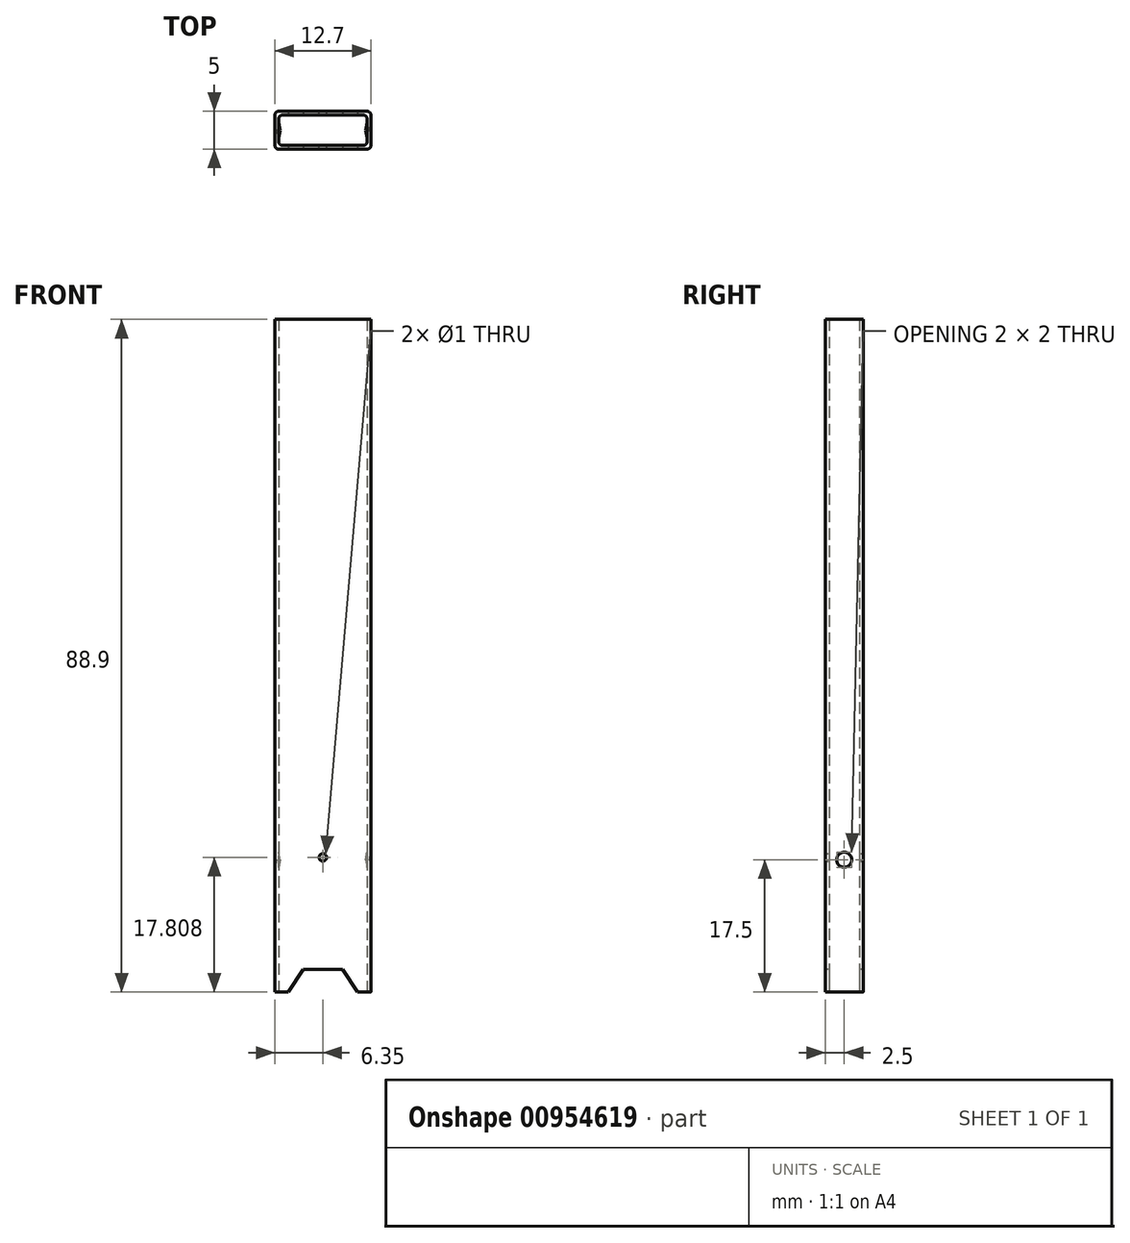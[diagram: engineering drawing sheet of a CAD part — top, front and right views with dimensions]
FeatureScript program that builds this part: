
annotation { "Feature Type Name" : "Feature", "Feature Type Description" : "" }
export const myFeature = defineFeature(function(context is Context, id is Id, definition is map)
    precondition{}
    {
        {
            var Q0;
            Q0=qCreatedBy(makeId("Top.planeOp"),FACE);
            var sketch = newSketch(context, id + "F0", { "sketchPlane" : qUnion([Q0])});
            skLineSegment(sketch, "E0.bottom", {"start": v(0.5, 0) * mm, "end": v(12.2, 0) * mm});
            skLineSegment(sketch, "E0.top", {"start": v(0.5, -5) * mm, "end": v(12.2, -5) * mm});
            skLineSegment(sketch, "E0.left", {"start": v(0, -0.5) * mm, "end": v(0, -4.5) * mm});
            skLineSegment(sketch, "E0.right", {"start": v(12.7, -0.5) * mm, "end": v(12.7, -4.5) * mm});
            skPoint(sketch, "E1.visualSharp", {"position": v(0, 0) * mm});
            skArc(sketch, "E1.filletArc", {"start": v(0.5, 0) * mm, "mid": v(0.15, -0.15) * mm, "end": v(0, -0.5) * mm});
            skPoint(sketch, "E2.visualSharp", {"position": v(0, -5) * mm});
            skArc(sketch, "E2.filletArc", {"start": v(0, -4.5) * mm, "mid": v(0.15, -4.85) * mm, "end": v(0.5, -5) * mm});
            skPoint(sketch, "E3.visualSharp", {"position": v(12.7, -5) * mm});
            skArc(sketch, "E3.filletArc", {"start": v(12.2, -5) * mm, "mid": v(12.55, -4.85) * mm, "end": v(12.7, -4.5) * mm});
            skPoint(sketch, "E4.visualSharp", {"position": v(12.7, 0) * mm});
            skArc(sketch, "E4.filletArc", {"start": v(12.7, -0.5) * mm, "mid": v(12.55, -0.15) * mm, "end": v(12.2, 0) * mm});
            skLineSegment(sketch, "E5.0", {"start": v(12.2, -0.5) * mm, "end": v(12.2, -0.5) * mm});
            skLineSegment(sketch, "E5.1", {"start": v(0.5, -0.5) * mm, "end": v(12.2, -0.5) * mm});
            skLineSegment(sketch, "E5.2", {"start": v(12.2, -0.5) * mm, "end": v(12.2, -4.5) * mm});
            skLineSegment(sketch, "E5.3", {"start": v(0.5, -0.5) * mm, "end": v(0.5, -0.5) * mm});
            skLineSegment(sketch, "E5.4", {"start": v(12.2, -4.5) * mm, "end": v(12.2, -4.5) * mm});
            skLineSegment(sketch, "E5.5", {"start": v(0.5, -4.5) * mm, "end": v(12.2, -4.5) * mm});
            skLineSegment(sketch, "E5.6", {"start": v(0.5, -4.5) * mm, "end": v(0.5, -4.5) * mm});
            skLineSegment(sketch, "E5.7", {"start": v(0.5, -0.5) * mm, "end": v(0.5, -4.5) * mm});
            skSolve(sketch);
        }
        {
            var Q0;
            Q0 = qSketchRegion(id + "F0", true);
            extrude(context, id + "F1", {"entities" : qUnion([Q0]), "depth" : 88.9 * mm, "offsetDistance" : 25 * mm});
        }
        {
            var Q0;
            Q0=makeQuery(id+"F1.opExtrude","SWEPT_FACE",FACE,{"disambiguationData":[OSD([sQuery(id+"F0.wireOp",EDGE,"E0.top")])]});
            var sketch = newSketch(context, id + "F2", { "sketchPlane" : qUnion([Q0])});
            skLineSegment(sketch, "E6", {"start": v(6.35, 0) * mm, "end": v(6.35, 10.65) * mm, "construction": true});
            skLineSegment(sketch, "E7", {"start": v(0, 0) * mm, "end": v(12.7, 0) * mm});
            skLineSegment(sketch, "E8", {"start": v(10.94, 0) * mm, "end": v(8.95, 3.03) * mm});
            skLineSegment(sketch, "E9", {"start": v(8.95, 3.03) * mm, "end": v(6.35, 3.03) * mm});
            skLineSegment(sketch, "E10.MirrorCS", {"start": v(1.76, 0) * mm, "end": v(3.75, 3.03) * mm});
            skLineSegment(sketch, "E11.MirrorCS", {"start": v(3.75, 3.03) * mm, "end": v(6.35, 3.03) * mm});
            skLineSegment(sketch, "E12", {"start": v(10.94, 0) * mm, "end": v(1.76, 0) * mm});
            skSolve(sketch);
        }
        {
            var Q0;
            Q0 = qSketchRegion(id + "F2", true);
            extrude(context, id + "F3", {"entities" : qUnion([Q0]), "operationType" : NewBodyOperationType.REMOVE, "oppositeDirection" : true, "depth" : 25 * mm, "offsetDistance" : 25 * mm});
        }
        {
            var Q0;
            Q0=makeQuery(id+"F1.opExtrude","SWEPT_FACE",FACE,{"disambiguationData":[OSD([sQuery(id+"F0.wireOp",EDGE,"E0.bottom")])]});
            var sketch = newSketch(context, id + "F4", { "sketchPlane" : qUnion([Q0])});
            skLineSegment(sketch, "E13", {"start": v(-6.35, 3.03) * mm, "end": v(-6.35, 17.8) * mm, "construction": true});
            skCircle(sketch, "E14", {"center": v(-6.35, 17.8) * mm, "radius": 0.5 * mm});
            skSolve(sketch);
        }
        {
            var Q0;
            Q0=makeQuery(id+"F4.imprint","IMPRINT",FACE,{"disambiguationData":[TD([[makeQuery(id+"F4.imprint","IMPRINT",EDGE,{"derivedFrom":sQuery(id+"F4.wireOp",EDGE,"E14")}),1.0]])]});
            extrude(context, id + "F5", {"entities" : qUnion([Q0]), "operationType" : NewBodyOperationType.REMOVE, "oppositeDirection" : true, "depth" : 25 * mm, "offsetDistance" : 25 * mm});
        }
        {
            var Q0;
            Q0=makeQuery(id+"F1.opExtrude","SWEPT_FACE",FACE,{"disambiguationData":[OSD([sQuery(id+"F0.wireOp",EDGE,"E0.right")])]});
            var sketch = newSketch(context, id + "F6", { "sketchPlane" : qUnion([Q0])});
            skLineSegment(sketch, "E15", {"start": v(-2.5, 0) * mm, "end": v(-2.5, 17.5) * mm, "construction": true});
            skCircle(sketch, "E16", {"center": v(-2.5, 17.5) * mm, "radius": 1 * mm});
            skSolve(sketch);
        }
        {
            var Q0;
            Q0 = qSketchRegion(id + "F6", true);
            extrude(context, id + "F7", {"entities" : qUnion([Q0]), "operationType" : NewBodyOperationType.REMOVE, "endBound" : BoundingType.THROUGH_ALL, "oppositeDirection" : true, "depth" : 25 * mm, "offsetDistance" : 25 * mm});
        }
        {
            var Q0;
            Q0=makeQuery(id+"F0.imprint","IMPRINT",FACE,{"disambiguationData":[TD([[makeQuery(id+"F0.imprint","IMPRINT",EDGE,{"derivedFrom":sQuery(id+"F0.wireOp",EDGE,"E0.bottom")}),-1.0]])]});
            cPlane(context, id + "F8", {"entities" : qUnion([Q0]), "cplaneType" : CPlaneType.OFFSET, "offset" : 17.5 * mm, "width" : 150 * mm, "height" : 150 * mm});
        }
        {
            var Q0;
            Q0=qCreatedBy(id+"F8.planeOp",FACE);
            var sketch = newSketch(context, id + "F9", { "sketchPlane" : qUnion([Q0])});
            skPoint(sketch, "E17.0", {"position": v(0, -2.5) * mm});
            skPoint(sketch, "E18", {"position": v(0, -1.5) * mm});
            skLineSegment(sketch, "E19", {"start": v(0, -2.5) * mm, "end": v(1.36, -2.5) * mm, "construction": true});
            skLineSegment(sketch, "E20", {"start": v(0, -1.5) * mm, "end": v(0.17, -2.5) * mm});
            skLineSegment(sketch, "E21", {"start": v(0.17, -2.5) * mm, "end": v(0.68, -2.5) * mm});
            skLineSegment(sketch, "E22", {"start": v(0.51, -1.5) * mm, "end": v(0.68, -2.5) * mm});
            skLineSegment(sketch, "E23", {"start": v(0.51, -1.5) * mm, "end": v(0, -1.5) * mm});
            skSolve(sketch);
        }
        {
            var Q0;
            Q0 = qSketchRegion(id + "F9", true);
            var Q1;
            Q1=sQuery(id+"F9.wireOp",EDGE,"E19");
            revolve(context, id + "F10", {"operationType" : NewBodyOperationType.ADD, "surfaceOperationType" : NewSurfaceOperationType.NEW, "entities" : qUnion([Q0]), "axis" : qUnion([Q1]), "revolveType" : RevolveType.FULL});
        }
        {
            var Q0;
            Q0=makeQuery(id+"F1.opExtrude","SWEPT_FACE",FACE,{"disambiguationData":[OSD([sQuery(id+"F0.wireOp",EDGE,"E0.right")])]});
            cPlane(context, id + "F11", {"entities" : qUnion([Q0]), "cplaneType" : CPlaneType.OFFSET, "offset" : 6.35 * mm, "oppositeDirection" : true, "width" : 150 * mm, "height" : 150 * mm});
        }
        {
            var Q0;
            Q0=makeQuery(id+"F1.opExtrude","SWEPT_BODY",BODY,{"disambiguationData":[OSD([sQuery(id+"F0.wireOp",EDGE,"E0.bottom"),sQuery(id+"F0.wireOp",EDGE,"E0.top"),sQuery(id+"F0.wireOp",EDGE,"E0.left"),sQuery(id+"F0.wireOp",EDGE,"E0.right"),sQuery(id+"F0.wireOp",EDGE,"E1.filletArc"),sQuery(id+"F0.wireOp",EDGE,"E2.filletArc"),sQuery(id+"F0.wireOp",EDGE,"E3.filletArc"),sQuery(id+"F0.wireOp",EDGE,"E4.filletArc"),sQuery(id+"F0.wireOp",EDGE,"E5.1"),sQuery(id+"F0.wireOp",EDGE,"E5.2"),sQuery(id+"F0.wireOp",EDGE,"E5.5"),sQuery(id+"F0.wireOp",EDGE,"E5.7")])]});
            var Q1;
            Q1=qCreatedBy(id+"F11.planeOp",FACE);
            mirror(context, id + "F12", {"operationType" : NewBodyOperationType.ADD, "entities" : qUnion([Q0]), "mirrorPlane" : qUnion([Q1])});
        }
        {
            var Q0;
            Q0=makeQuery(id+"F1.opExtrude","SWEPT_EDGE",EDGE,{"disambiguationData":[OSD([sQuery(id+"F0.wireOp",EDGE,"E5.2"),sQuery(id+"F0.wireOp",EDGE,"E5.5")])]});
            var Q1;
            Q1=makeQuery(id+"F1.opExtrude","SWEPT_EDGE",EDGE,{"disambiguationData":[OSD([sQuery(id+"F0.wireOp",EDGE,"E5.5"),sQuery(id+"F0.wireOp",EDGE,"E5.7")])]});
            var Q2;
            Q2=makeQuery(id+"F1.opExtrude","SWEPT_EDGE",EDGE,{"disambiguationData":[OSD([sQuery(id+"F0.wireOp",EDGE,"E5.1"),sQuery(id+"F0.wireOp",EDGE,"E5.7")])]});
            var Q3;
            Q3=makeQuery(id+"F1.opExtrude","SWEPT_EDGE",EDGE,{"disambiguationData":[OSD([sQuery(id+"F0.wireOp",EDGE,"E5.1"),sQuery(id+"F0.wireOp",EDGE,"E5.2")])]});
            fillet(context, id + "F13", {"entities" : qUnion([Q0, Q1, Q2, Q3]), "radius" : 0.5 * mm, "tangentPropagation" : true, "allowEdgeOverflow" : false});
        }
    });
